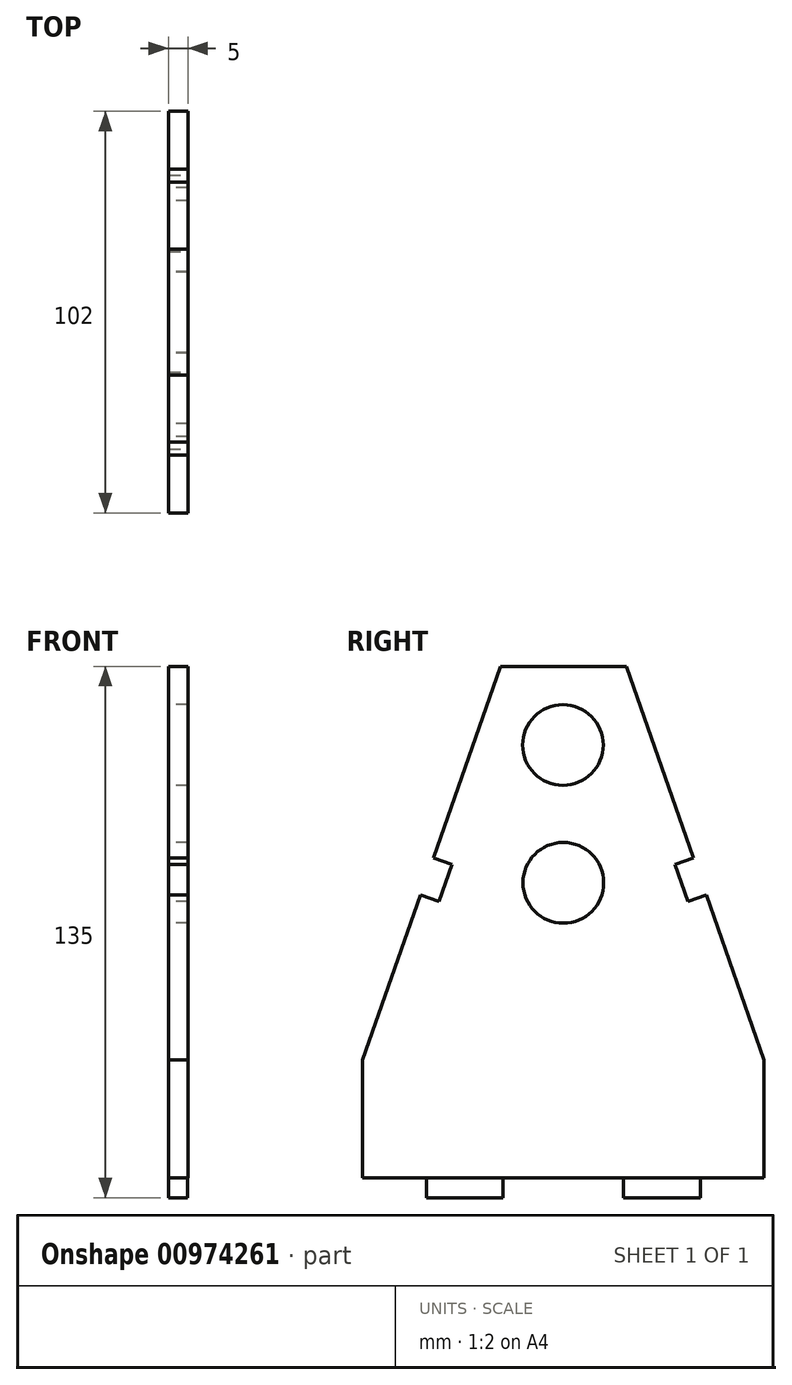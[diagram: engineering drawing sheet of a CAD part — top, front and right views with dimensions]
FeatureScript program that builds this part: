
annotation { "Feature Type Name" : "Feature", "Feature Type Description" : "" }
export const myFeature = defineFeature(function(context is Context, id is Id, definition is map)
    precondition{}
    {
        {
            var Q0;
            Q0=qCreatedBy(makeId("Top.planeOp"),FACE);
            var sketch = newSketch(context, id + "F0", { "sketchPlane" : qUnion([Q0])});
            skLineSegment(sketch, "E0", {"start": v(0, 51.11) * mm, "end": v(0, -50.89) * mm});
            skLineSegment(sketch, "E1", {"start": v(5, 51.11) * mm, "end": v(5, -50.89) * mm});
            skLineSegment(sketch, "E2", {"start": v(0, 51.11) * mm, "end": v(5, 51.11) * mm});
            skLineSegment(sketch, "E3", {"start": v(0, -50.89) * mm, "end": v(5, -50.89) * mm});
            skSolve(sketch);
        }
        {
            var Q0;
            Q0=makeQuery(id+"F0.imprint","IMPRINT",FACE,{"disambiguationData":[TD([[makeQuery(id+"F0.imprint","IMPRINT",EDGE,{"derivedFrom":sQuery(id+"F0.wireOp",EDGE,"E0")}),1.0]])]});
            extrude(context, id + "F1", {"entities" : qUnion([Q0]), "depth" : 130 * mm, "offsetDistance" : 25 * mm});
        }
        {
            var Q0;
            Q0=makeQuery(id+"F1.opExtrude","CAP_EDGE",EDGE,{"disambiguationData":[OSD([sQuery(id+"F0.wireOp",EDGE,"E3")])],"isStart":false});
            var Q1;
            Q1=makeQuery(id+"F1.opExtrude","CAP_EDGE",EDGE,{"disambiguationData":[OSD([sQuery(id+"F0.wireOp",EDGE,"E2")])],"isStart":false});
            chamfer(context, id + "F2", {"entities" : qUnion([Q0, Q1]), "chamferType" : ChamferType.TWO_OFFSETS, "width1" : 35 * mm, "oppositeDirection" : false, "width2" : 100 * mm, "tangentPropagation" : true});
        }
        {
            var Q0;
            Q0=makeQuery(id+"F1.opExtrude","SWEPT_FACE",FACE,{"disambiguationData":[OSD([sQuery(id+"F0.wireOp",EDGE,"E0")])]});
            var sketch = newSketch(context, id + "F3", { "sketchPlane" : qUnion([Q0])});
            skLineSegment(sketch, "E4", {"start": v(-51.11, 0) * mm, "end": v(50.89, 0) * mm, "construction": true});
            skLineSegment(sketch, "E5", {"start": v(-51.11, 75) * mm, "end": v(50.89, 75) * mm, "construction": true});
            skLineSegment(sketch, "E6", {"start": v(0, 0) * mm, "end": v(-0.11, 75) * mm, "construction": true});
            skPoint(sketch, "E6.endSnap0", {"position": v(-0.11, 75) * mm});
            skLineSegment(sketch, "E7", {"start": v(50.89, 110) * mm, "end": v(-51.11, 110) * mm, "construction": true});
            skLineSegment(sketch, "E8", {"start": v(-0.11, 75) * mm, "end": v(0, 110) * mm, "construction": true});
            skPoint(sketch, "E9", {"position": v(0, 110) * mm});
            skLineSegment(sketch, "E10", {"start": v(10.6, 130) * mm, "end": v(50.89, 14.86) * mm, "construction": true});
            skLineSegment(sketch, "E11", {"start": v(29.84, 75) * mm, "end": v(34.56, 76.65) * mm});
            skLineSegment(sketch, "E12", {"start": v(32.9, 81.37) * mm, "end": v(28.19, 79.72) * mm});
            skLineSegment(sketch, "E13", {"start": v(36.21, 71.93) * mm, "end": v(31.5, 70.28) * mm});
            skLineSegment(sketch, "E14", {"start": v(28.19, 79.72) * mm, "end": v(31.5, 70.28) * mm});
            skLineSegment(sketch, "E15", {"start": v(-10.81, 130) * mm, "end": v(-51.11, 14.86) * mm, "construction": true});
            skLineSegment(sketch, "E16", {"start": v(-30.06, 75) * mm, "end": v(-34.78, 76.65) * mm, "construction": true});
            skLineSegment(sketch, "E17", {"start": v(-28.41, 79.72) * mm, "end": v(-33.13, 81.37) * mm});
            skLineSegment(sketch, "E18", {"start": v(-31.72, 70.28) * mm, "end": v(-36.43, 71.93) * mm});
            skLineSegment(sketch, "E19", {"start": v(-28.41, 79.72) * mm, "end": v(-30.06, 75) * mm});
            skLineSegment(sketch, "E20", {"start": v(-31.72, 70.28) * mm, "end": v(-30.06, 75) * mm});
            skSolve(sketch);
        }
        {
            var Q0;
            Q0=makeQuery(id+"F1.opExtrude","CAP_FACE",FACE,{"disambiguationData":[OSD([sQuery(id+"F0.wireOp",EDGE,"E0"),sQuery(id+"F0.wireOp",EDGE,"E1"),sQuery(id+"F0.wireOp",EDGE,"E2"),sQuery(id+"F0.wireOp",EDGE,"E3")])],"isStart":true});
            var sketch = newSketch(context, id + "F4", { "sketchPlane" : qUnion([Q0])});
            skLineSegment(sketch, "E21.MirrorCS", {"start": v(-6.9, -15.41) * mm, "end": v(13.87, -15.41) * mm});
            skLineSegment(sketch, "E22.MirrorCS", {"start": v(-6.9, -34.91) * mm, "end": v(13.87, -34.91) * mm});
            skLineSegment(sketch, "E23", {"start": v(0, 50.89) * mm, "end": v(0, -51.11) * mm});
            skLineSegment(sketch, "E24", {"start": v(5, 50.89) * mm, "end": v(5, -51.11) * mm});
            skLineSegment(sketch, "E25", {"start": v(0.1, 50.89) * mm, "end": v(0.1, -51.11) * mm});
            skLineSegment(sketch, "E26", {"start": v(4.9, -51.11) * mm, "end": v(4.9, 50.89) * mm});
            skLineSegment(sketch, "E27", {"start": v(-6.9, 34.69) * mm, "end": v(13.87, 34.69) * mm});
            skLineSegment(sketch, "E28", {"start": v(-6.9, 15.19) * mm, "end": v(13.87, 15.19) * mm});
            skSolve(sketch);
        }
        {
            var Q0;
            {var subQ0=sQuery(id+"F4.wireOp",EDGE,"E25");var subQ1=sQuery(id+"F4.wireOp",EDGE,"DMbmTyNS-WR5i-p7ep-R4Gh-vyUju3U0aCHA");var subQ2=makeQuery(id+"F4.imprint","INTERSECT",VERTEX,{"derivedFrom":[subQ1,subQ0]});Q0=makeQuery(id+"F4.imprint","IMPRINT",FACE,{"disambiguationData":[TD([[makeQuery(id+"F4.imprint","IMPRINT",EDGE,{"disambiguationData":[TD([[subQ2,-1.0]])],"derivedFrom":subQ1}),-1.0]])]});}
            var Q1;
            {var subQ0=sQuery(id+"F4.wireOp",EDGE,"E25");var subQ1=sQuery(id+"F4.wireOp",EDGE,"E21.MirrorCS");var subQ2=makeQuery(id+"F4.imprint","INTERSECT",VERTEX,{"derivedFrom":[subQ1,subQ0]});Q1=makeQuery(id+"F4.imprint","IMPRINT",FACE,{"disambiguationData":[TD([[makeQuery(id+"F4.imprint","IMPRINT",EDGE,{"disambiguationData":[TD([[subQ2,-1.0]])],"derivedFrom":subQ1}),-1.0]])]});}
            var Q2;
            {var subQ0=sQuery(id+"F4.wireOp",EDGE,"E27");var subQ1=sQuery(id+"F4.wireOp",EDGE,"E25");var subQ2=makeQuery(id+"F4.imprint","INTERSECT",VERTEX,{"derivedFrom":[subQ1,subQ0]});Q2=makeQuery(id+"F4.imprint","IMPRINT",FACE,{"disambiguationData":[TD([[makeQuery(id+"F4.imprint","IMPRINT",EDGE,{"disambiguationData":[TD([[subQ2,-1.0]])],"derivedFrom":subQ1}),1.0]])]});}
            extrude(context, id + "F5", {"entities" : qUnion([Q0, Q1, Q2]), "operationType" : NewBodyOperationType.ADD, "depth" : 5 * mm, "offsetDistance" : 25 * mm});
        }
        {
            var Q0;
            Q0=sQuery(id+"F3.wireOp",VERTEX,"E6.endSnap0");
            var Q1;
            Q1=makeQuery(id+"F1.opExtrude","SWEPT_BODY",BODY,{"disambiguationData":[OSD([sQuery(id+"F0.wireOp",EDGE,"E0"),sQuery(id+"F0.wireOp",EDGE,"E1"),sQuery(id+"F0.wireOp",EDGE,"E2"),sQuery(id+"F0.wireOp",EDGE,"E3")])]});
            hole(context, id + "F6", {"style" : HoleStyle.SIMPLE, "endStyle" : HoleEndStyle.THROUGH, "holeDiameter" : 20.5 * mm, "majorDiameter" : 5 * mm, "isTappedThrough" : true, "tappedDepth" : 12 * mm, "tapClearance" : 3, "locations" : qUnion([Q0]), "scope" : qUnion([Q1])});
        }
        {
            var Q0;
            Q0=sQuery(id+"F3.wireOp",VERTEX,"E9");
            var Q1;
            Q1=makeQuery(id+"F1.opExtrude","SWEPT_BODY",BODY,{"disambiguationData":[OSD([sQuery(id+"F0.wireOp",EDGE,"E0"),sQuery(id+"F0.wireOp",EDGE,"E1"),sQuery(id+"F0.wireOp",EDGE,"E2"),sQuery(id+"F0.wireOp",EDGE,"E3")])]});
            hole(context, id + "F7", {"style" : HoleStyle.SIMPLE, "endStyle" : HoleEndStyle.THROUGH, "holeDiameter" : 20.5 * mm, "majorDiameter" : 5 * mm, "isTappedThrough" : true, "tappedDepth" : 12 * mm, "tapClearance" : 3, "locations" : qUnion([Q0]), "scope" : qUnion([Q1])});
        }
        {
            var Q0;
            {var subQ1=sQuery(id+"F3.wireOp",EDGE,"E17");Q0=makeQuery(id+"F3.imprint","IMPRINT",FACE,{"disambiguationData":[TD([[makeQuery(id+"F3.imprint","IMPRINT",EDGE,{"derivedFrom":subQ1}),1.0]])]});}
            var Q1;
            {var subQ0=sQuery(id+"F3.wireOp",EDGE,"E11");Q1=makeQuery(id+"F3.imprint","IMPRINT",FACE,{"disambiguationData":[TD([[makeQuery(id+"F3.imprint","IMPRINT",EDGE,{"derivedFrom":subQ0}),1.0]])]});}
            var Q2;
            {var subQ0=sQuery(id+"F3.wireOp",EDGE,"E11");Q2=makeQuery(id+"F3.imprint","IMPRINT",FACE,{"disambiguationData":[TD([[makeQuery(id+"F3.imprint","IMPRINT",EDGE,{"derivedFrom":subQ0}),-1.0]])]});}
            extrude(context, id + "F8", {"entities" : qUnion([Q0, Q1, Q2]), "operationType" : NewBodyOperationType.REMOVE, "oppositeDirection" : true, "depth" : 25 * mm, "offsetDistance" : 25 * mm});
        }
    });
